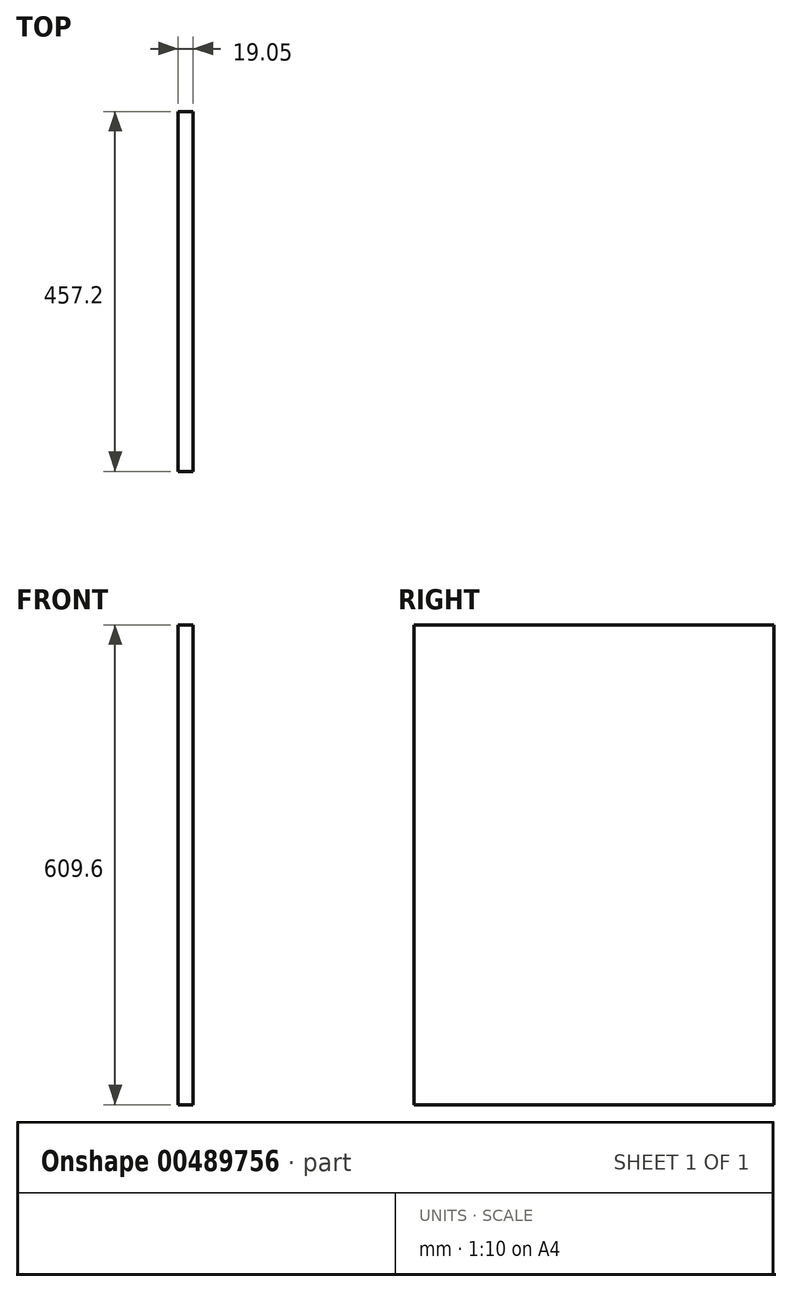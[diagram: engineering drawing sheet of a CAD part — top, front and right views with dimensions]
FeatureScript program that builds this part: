
annotation { "Feature Type Name" : "Feature", "Feature Type Description" : "" }
export const myFeature = defineFeature(function(context is Context, id is Id, definition is map)
    precondition{}
    {
        {
            var Q0;
            Q0=qCreatedBy(makeId("Right.planeOp"),FACE);
            var sketch = newSketch(context, id + "F0", { "sketchPlane" : qUnion([Q0])});
            skLineSegment(sketch, "E0.bottom", {"start": v(-228.42, 390.96) * mm, "end": v(228.78, 390.96) * mm});
            skLineSegment(sketch, "E0.top", {"start": v(-228.42, -218.64) * mm, "end": v(228.78, -218.64) * mm});
            skLineSegment(sketch, "E0.left", {"start": v(-228.42, 390.96) * mm, "end": v(-228.42, -218.64) * mm});
            skLineSegment(sketch, "E0.right", {"start": v(228.78, 390.96) * mm, "end": v(228.78, -218.64) * mm});
            skSolve(sketch);
        }
        {
            var Q0;
            Q0=makeQuery(id+"F0.imprint","IMPRINT",FACE,{"disambiguationData":[TD([[makeQuery(id+"F0.imprint","IMPRINT",EDGE,{"derivedFrom":sQuery(id+"F0.wireOp",EDGE,"E0.bottom")}),-1.0]])]});
            extrude(context, id + "F1", {"entities" : qUnion([Q0]), "depth" : 19.05 * mm});
        }
    });
